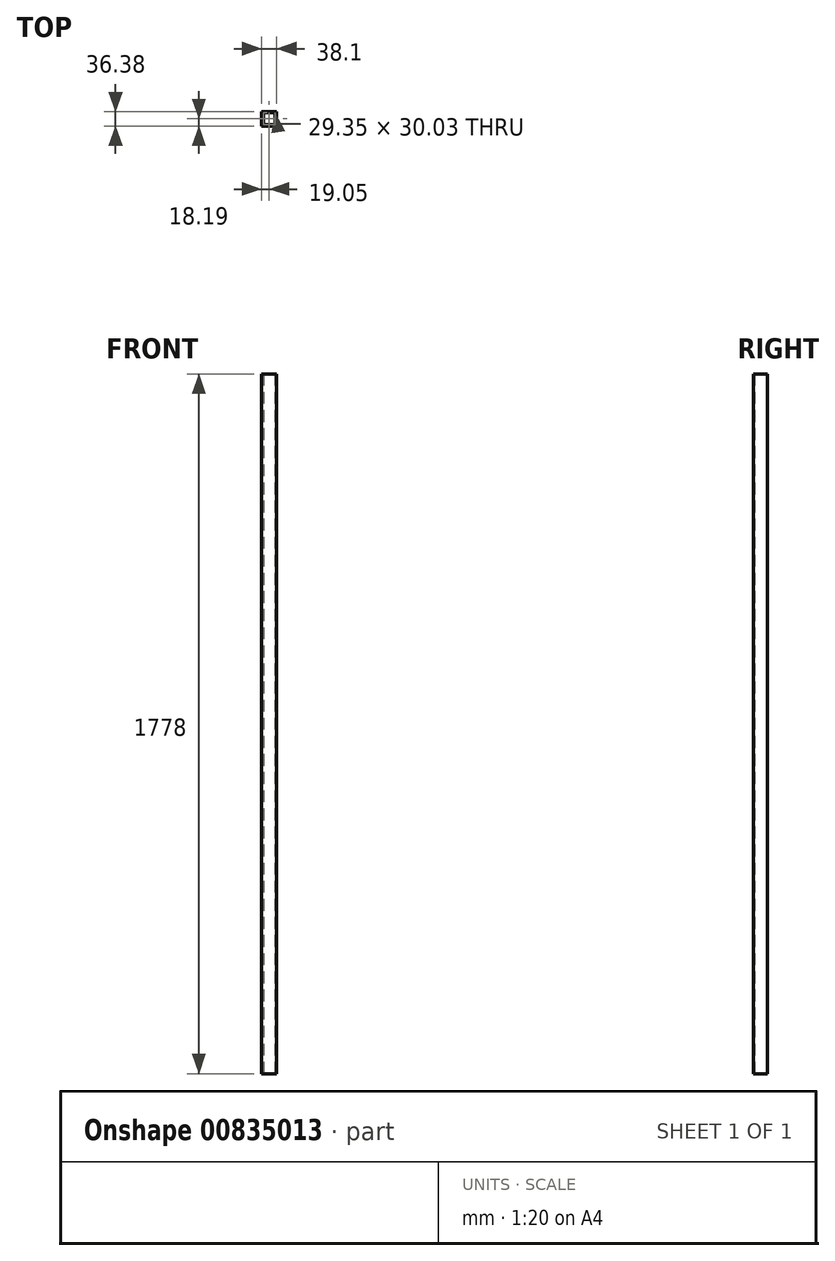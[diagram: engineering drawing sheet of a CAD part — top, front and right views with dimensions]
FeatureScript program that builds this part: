
annotation { "Feature Type Name" : "Feature", "Feature Type Description" : "" }
export const myFeature = defineFeature(function(context is Context, id is Id, definition is map)
    precondition{}
    {
        {
            var Q0;
            Q0=qCreatedBy(makeId("Top.planeOp"),FACE);
            var sketch = newSketch(context, id + "F0", { "sketchPlane" : qUnion([Q0])});
            skLineSegment(sketch, "E0.bottom", {"start": v(19.05, 18.19) * mm, "end": v(-19.05, 18.19) * mm});
            skLineSegment(sketch, "E0.top", {"start": v(19.05, -18.19) * mm, "end": v(-19.05, -18.19) * mm});
            skLineSegment(sketch, "E0.left", {"start": v(19.05, 18.19) * mm, "end": v(19.05, -18.19) * mm});
            skLineSegment(sketch, "E0.right", {"start": v(-19.05, 18.19) * mm, "end": v(-19.05, -18.19) * mm});
            skPoint(sketch, "E0.middle", {"position": v(0, 0) * mm});
            skLineSegment(sketch, "E1.bottom", {"start": v(14.68, 15.01) * mm, "end": v(-14.68, 15.01) * mm});
            skLineSegment(sketch, "E1.top", {"start": v(14.68, -15.01) * mm, "end": v(-14.68, -15.01) * mm});
            skLineSegment(sketch, "E1.left", {"start": v(14.68, 15.01) * mm, "end": v(14.68, -15.01) * mm});
            skLineSegment(sketch, "E1.right", {"start": v(-14.68, 15.01) * mm, "end": v(-14.68, -15.01) * mm});
            skSolve(sketch);
        }
        {
            var Q0;
            Q0=makeQuery(id+"F0.imprint","IMPRINT",FACE,{"disambiguationData":[TD([[makeQuery(id+"F0.imprint","IMPRINT",EDGE,{"derivedFrom":sQuery(id+"F0.wireOp",EDGE,"E0.bottom")}),1.0]])]});
            extrude(context, id + "F1", {"entities" : qUnion([Q0]), "endBound" : BoundingType.SYMMETRIC, "depth" : 1778 * mm, "offsetDistance" : 25.4 * mm});
        }
    });
